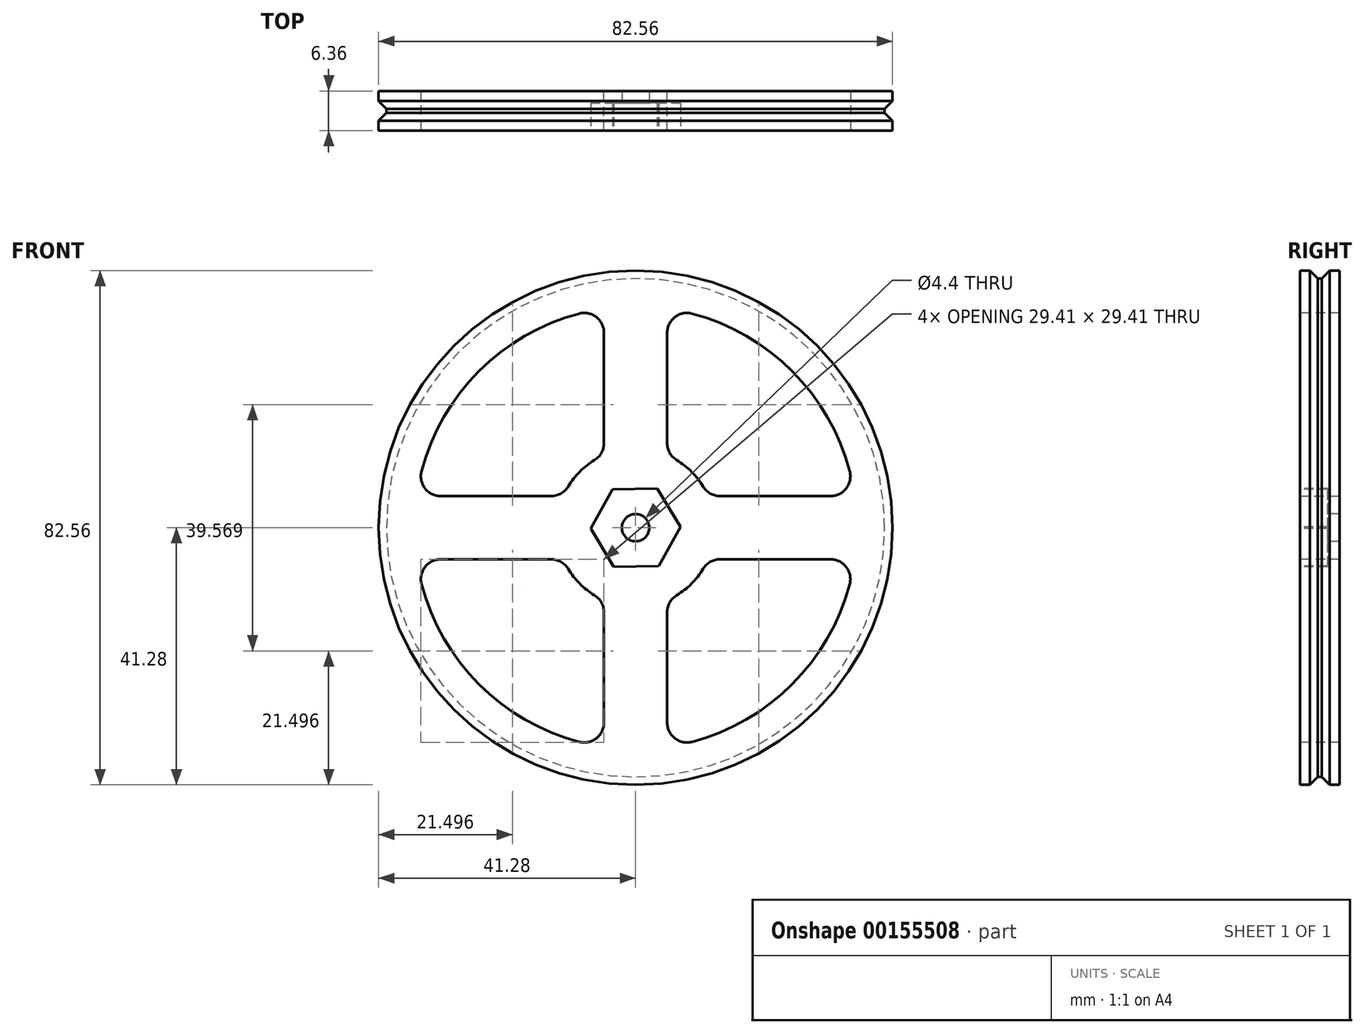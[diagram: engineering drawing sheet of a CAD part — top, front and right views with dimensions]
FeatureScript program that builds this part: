
annotation { "Feature Type Name" : "Feature", "Feature Type Description" : "" }
export const myFeature = defineFeature(function(context is Context, id is Id, definition is map)
    precondition{}
    {
        {
            var Q0;
            Q0=qCreatedBy(makeId("Front.planeOp"),FACE);
            var sketch = newSketch(context, id + "F0", { "sketchPlane" : qUnion([Q0])});
            skCircle(sketch, "E0", {"center": v(0, 0) * mm, "radius": 40 * mm});
            skCircle(sketch, "E1.0", {"center": v(0, 0) * mm, "radius": 41.28 * mm});
            skCircle(sketch, "E2.cCircle", {"center": v(0, 0) * mm, "radius": 6.35 * mm, "construction": true});
            skLineSegment(sketch, "E2.0", {"start": v(-3.67, 6.35) * mm, "end": v(3.67, 6.35) * mm});
            skLineSegment(sketch, "E2.1", {"start": v(3.67, 6.35) * mm, "end": v(7.33, 0) * mm});
            skLineSegment(sketch, "E2.2", {"start": v(7.33, 0) * mm, "end": v(3.67, -6.35) * mm});
            skLineSegment(sketch, "E2.3", {"start": v(3.67, -6.35) * mm, "end": v(-3.67, -6.35) * mm});
            skLineSegment(sketch, "E2.4", {"start": v(-3.67, -6.35) * mm, "end": v(-7.33, 0) * mm});
            skLineSegment(sketch, "E2.5", {"start": v(-7.33, 0) * mm, "end": v(-3.67, 6.35) * mm});
            skPoint(sketch, "E2.0.midPoint", {"position": v(0, 6.35) * mm});
            skSolve(sketch);
        }
        {
            var Q0;
            Q0=makeQuery(id+"F0.imprint","IMPRINT",FACE,{"disambiguationData":[TD([[makeQuery(id+"F0.imprint","IMPRINT",EDGE,{"derivedFrom":sQuery(id+"F0.wireOp",EDGE,"E0")}),1.0]])]});
            var Q1;
            Q1=makeQuery(id+"F0.imprint","IMPRINT",FACE,{"disambiguationData":[TD([[makeQuery(id+"F0.imprint","IMPRINT",EDGE,{"derivedFrom":sQuery(id+"F0.wireOp",EDGE,"E0")}),-1.0]])]});
            var Q2;
            Q2=makeQuery(id+"F0.imprint","IMPRINT",FACE,{"disambiguationData":[TD([[makeQuery(id+"F0.imprint","IMPRINT",EDGE,{"derivedFrom":sQuery(id+"F0.wireOp",EDGE,"E2.0")}),-1.0]])]});
            extrude(context, id + "F1", {"entities" : qUnion([Q0, Q1, Q2]), "endBound" : BoundingType.SYMMETRIC, "depth" : 6.35 * mm});
        }
        {
            var Q0;
            Q0=makeQuery(id+"F1.opExtrude","CAP_FACE",FACE,{"disambiguationData":[OSD([sQuery(id+"F0.wireOp",EDGE,"E1.0")])],"isStart":false});
            var sketch = newSketch(context, id + "F2", { "sketchPlane" : qUnion([Q0])});
            skCircle(sketch, "E3.cCircle", {"center": v(0, 0) * mm, "radius": 6.22 * mm, "construction": true});
            skLineSegment(sketch, "E3.0", {"start": v(3.49, 6.28) * mm, "end": v(7.18, 0.12) * mm});
            skLineSegment(sketch, "E3.1", {"start": v(7.18, 0.12) * mm, "end": v(3.7, -6.16) * mm});
            skLineSegment(sketch, "E3.2", {"start": v(3.7, -6.16) * mm, "end": v(-3.49, -6.28) * mm});
            skLineSegment(sketch, "E3.3", {"start": v(-3.49, -6.28) * mm, "end": v(-7.18, -0.12) * mm});
            skLineSegment(sketch, "E3.4", {"start": v(-7.18, -0.12) * mm, "end": v(-3.7, 6.16) * mm});
            skLineSegment(sketch, "E3.5", {"start": v(-3.7, 6.16) * mm, "end": v(3.49, 6.28) * mm});
            skPoint(sketch, "E3.0.midPoint", {"position": v(5.34, 3.2) * mm});
            skSolve(sketch);
        }
        {
            var Q0;
            Q0 = qSketchRegion(id + "F2", true);
            extrude(context, id + "F3", {"entities" : qUnion([Q0]), "operationType" : NewBodyOperationType.REMOVE, "oppositeDirection" : true, "depth" : 4.44 * mm});
        }
        {
            var Q0;
            Q0=makeQuery(id+"F1.opExtrude","CAP_FACE",FACE,{"disambiguationData":[OSD([sQuery(id+"F0.wireOp",EDGE,"E1.0"),sQuery(id+"F0.wireOp",EDGE,"E2.0"),sQuery(id+"F0.wireOp",EDGE,"E2.1"),sQuery(id+"F0.wireOp",EDGE,"E2.2"),sQuery(id+"F0.wireOp",EDGE,"E2.3"),sQuery(id+"F0.wireOp",EDGE,"E2.4"),sQuery(id+"F0.wireOp",EDGE,"E2.5")])],"isStart":false});
            var sketch = newSketch(context, id + "F4", { "sketchPlane" : qUnion([Q0])});
            skCircle(sketch, "E4", {"center": v(0, 0) * mm, "radius": 35.56 * mm});
            skCircle(sketch, "E5.0", {"center": v(0, 0) * mm, "radius": 12.7 * mm});
            skLineSegment(sketch, "E6", {"start": v(0, -12.7) * mm, "end": v(0, -35.56) * mm});
            skLineSegment(sketch, "E7.0", {"start": v(-5.08, -11.64) * mm, "end": v(-5.08, -35.2) * mm});
            skLineSegment(sketch, "E8.0", {"start": v(5.08, -11.64) * mm, "end": v(5.08, -35.2) * mm});
            skLineSegment(sketch, "E9.1.0", {"start": v(11.64, -5.08) * mm, "end": v(35.2, -5.08) * mm});
            skLineSegment(sketch, "E9.1.1", {"start": v(11.64, 5.08) * mm, "end": v(35.2, 5.08) * mm});
            skLineSegment(sketch, "E9.2.0", {"start": v(5.08, 11.64) * mm, "end": v(5.08, 35.2) * mm});
            skLineSegment(sketch, "E9.2.1", {"start": v(-5.08, 11.64) * mm, "end": v(-5.08, 35.2) * mm});
            skLineSegment(sketch, "E9.3.0", {"start": v(-11.64, 5.08) * mm, "end": v(-35.2, 5.08) * mm});
            skLineSegment(sketch, "E9.3.1", {"start": v(-11.64, -5.08) * mm, "end": v(-35.2, -5.08) * mm});
            skSolve(sketch);
        }
        {
            var Q0;
            {var subQ0=sQuery(id+"F4.wireOp",EDGE,"E7.0");Q0=makeQuery(id+"F4.imprint","IMPRINT",FACE,{"disambiguationData":[TD([[makeQuery(id+"F4.imprint","IMPRINT",EDGE,{"derivedFrom":subQ0}),-1.0]])]});}
            var Q1;
            {var subQ0=sQuery(id+"F4.wireOp",EDGE,"E9.2.1");Q1=makeQuery(id+"F4.imprint","IMPRINT",FACE,{"disambiguationData":[TD([[makeQuery(id+"F4.imprint","IMPRINT",EDGE,{"derivedFrom":subQ0}),1.0]])]});}
            var Q2;
            {var subQ0=sQuery(id+"F4.wireOp",EDGE,"E9.1.1");Q2=makeQuery(id+"F4.imprint","IMPRINT",FACE,{"disambiguationData":[TD([[makeQuery(id+"F4.imprint","IMPRINT",EDGE,{"derivedFrom":subQ0}),1.0]])]});}
            var Q3;
            {var subQ0=sQuery(id+"F4.wireOp",EDGE,"E8.0");Q3=makeQuery(id+"F4.imprint","IMPRINT",FACE,{"disambiguationData":[TD([[makeQuery(id+"F4.imprint","IMPRINT",EDGE,{"derivedFrom":subQ0}),1.0]])]});}
            extrude(context, id + "F5", {"entities" : qUnion([Q0, Q1, Q2, Q3]), "operationType" : NewBodyOperationType.REMOVE, "endBound" : BoundingType.THROUGH_ALL, "oppositeDirection" : true, "depth" : 25.4 * mm});
        }
        {
            var Q0;
            Q0=makeQuery(id+"F5.boolean.opBoolean","COPY",EDGE,{"derivedFrom":makeQuery(id+"F5.opExtrude","SWEPT_EDGE",EDGE,{"disambiguationData":[OSD([sQuery(id+"F4.wireOp",EDGE,"E4"),sQuery(id+"F4.wireOp",EDGE,"27957d35-a56d-4cfa-9457-b1a0cf56e145.3.0")])]})});
            var Q1;
            Q1=makeQuery(id+"F5.boolean.opBoolean","COPY",EDGE,{"derivedFrom":makeQuery(id+"F5.opExtrude","SWEPT_EDGE",EDGE,{"disambiguationData":[OSD([sQuery(id+"F4.wireOp",EDGE,"E4"),sQuery(id+"F4.wireOp",EDGE,"e348a229-b992-494f-8d39-545bbdace99f.0")])]})});
            var Q2;
            Q2=makeQuery(id+"F5.boolean.opBoolean","COPY",EDGE,{"derivedFrom":makeQuery(id+"F5.opExtrude","SWEPT_EDGE",EDGE,{"disambiguationData":[OSD([sQuery(id+"F4.wireOp",EDGE,"E5.0"),sQuery(id+"F4.wireOp",EDGE,"27957d35-a56d-4cfa-9457-b1a0cf56e145.1.1")])]})});
            var Q3;
            Q3=makeQuery(id+"F5.boolean.opBoolean","COPY",EDGE,{"derivedFrom":makeQuery(id+"F5.opExtrude","SWEPT_EDGE",EDGE,{"disambiguationData":[OSD([sQuery(id+"F4.wireOp",EDGE,"E5.0"),sQuery(id+"F4.wireOp",EDGE,"27957d35-a56d-4cfa-9457-b1a0cf56e145.2.0")])]})});
            var Q4;
            Q4=makeQuery(id+"F5.boolean.opBoolean","COPY",EDGE,{"derivedFrom":makeQuery(id+"F5.opExtrude","SWEPT_EDGE",EDGE,{"disambiguationData":[OSD([sQuery(id+"F4.wireOp",EDGE,"E4"),sQuery(id+"F4.wireOp",EDGE,"27957d35-a56d-4cfa-9457-b1a0cf56e145.2.1")])]})});
            var Q5;
            Q5=makeQuery(id+"F5.boolean.opBoolean","COPY",EDGE,{"derivedFrom":makeQuery(id+"F5.opExtrude","SWEPT_EDGE",EDGE,{"disambiguationData":[OSD([sQuery(id+"F4.wireOp",EDGE,"E5.0"),sQuery(id+"F4.wireOp",EDGE,"27957d35-a56d-4cfa-9457-b1a0cf56e145.2.1")])]})});
            var Q6;
            Q6=makeQuery(id+"F5.boolean.opBoolean","COPY",EDGE,{"derivedFrom":makeQuery(id+"F5.opExtrude","SWEPT_EDGE",EDGE,{"disambiguationData":[OSD([sQuery(id+"F4.wireOp",EDGE,"E4"),sQuery(id+"F4.wireOp",EDGE,"27957d35-a56d-4cfa-9457-b1a0cf56e145.2.0")])]})});
            var Q7;
            Q7=makeQuery(id+"F5.boolean.opBoolean","COPY",EDGE,{"derivedFrom":makeQuery(id+"F5.opExtrude","SWEPT_EDGE",EDGE,{"disambiguationData":[OSD([sQuery(id+"F4.wireOp",EDGE,"E4"),sQuery(id+"F4.wireOp",EDGE,"27957d35-a56d-4cfa-9457-b1a0cf56e145.1.1")])]})});
            var Q8;
            Q8=makeQuery(id+"F5.boolean.opBoolean","COPY",EDGE,{"derivedFrom":makeQuery(id+"F5.opExtrude","SWEPT_EDGE",EDGE,{"disambiguationData":[OSD([sQuery(id+"F4.wireOp",EDGE,"E4"),sQuery(id+"F4.wireOp",EDGE,"27957d35-a56d-4cfa-9457-b1a0cf56e145.1.0")])]})});
            var Q9;
            Q9=makeQuery(id+"F5.boolean.opBoolean","COPY",EDGE,{"derivedFrom":makeQuery(id+"F5.opExtrude","SWEPT_EDGE",EDGE,{"disambiguationData":[OSD([sQuery(id+"F4.wireOp",EDGE,"E5.0"),sQuery(id+"F4.wireOp",EDGE,"27957d35-a56d-4cfa-9457-b1a0cf56e145.3.1")])]})});
            var Q10;
            Q10=makeQuery(id+"F5.boolean.opBoolean","COPY",EDGE,{"derivedFrom":makeQuery(id+"F5.opExtrude","SWEPT_EDGE",EDGE,{"disambiguationData":[OSD([sQuery(id+"F4.wireOp",EDGE,"E5.0"),sQuery(id+"F4.wireOp",EDGE,"0dbcb386-fed9-4ae0-a355-918e704f70ac.0")])]})});
            var Q11;
            Q11=makeQuery(id+"F5.boolean.opBoolean","COPY",EDGE,{"derivedFrom":makeQuery(id+"F5.opExtrude","SWEPT_EDGE",EDGE,{"disambiguationData":[OSD([sQuery(id+"F4.wireOp",EDGE,"E4"),sQuery(id+"F4.wireOp",EDGE,"0dbcb386-fed9-4ae0-a355-918e704f70ac.0")])]})});
            var Q12;
            Q12=makeQuery(id+"F5.boolean.opBoolean","COPY",EDGE,{"derivedFrom":makeQuery(id+"F5.opExtrude","SWEPT_EDGE",EDGE,{"disambiguationData":[OSD([sQuery(id+"F4.wireOp",EDGE,"E4"),sQuery(id+"F4.wireOp",EDGE,"27957d35-a56d-4cfa-9457-b1a0cf56e145.3.1")])]})});
            var Q13;
            Q13=makeQuery(id+"F5.boolean.opBoolean","COPY",EDGE,{"derivedFrom":makeQuery(id+"F5.opExtrude","SWEPT_EDGE",EDGE,{"disambiguationData":[OSD([sQuery(id+"F4.wireOp",EDGE,"E5.0"),sQuery(id+"F4.wireOp",EDGE,"27957d35-a56d-4cfa-9457-b1a0cf56e145.3.0")])]})});
            var Q14;
            Q14=makeQuery(id+"F5.boolean.opBoolean","COPY",EDGE,{"derivedFrom":makeQuery(id+"F5.opExtrude","SWEPT_EDGE",EDGE,{"disambiguationData":[OSD([sQuery(id+"F4.wireOp",EDGE,"E5.0"),sQuery(id+"F4.wireOp",EDGE,"e348a229-b992-494f-8d39-545bbdace99f.0")])]})});
            var Q15;
            Q15=makeQuery(id+"F5.boolean.opBoolean","COPY",EDGE,{"derivedFrom":makeQuery(id+"F5.opExtrude","SWEPT_EDGE",EDGE,{"disambiguationData":[OSD([sQuery(id+"F4.wireOp",EDGE,"E5.0"),sQuery(id+"F4.wireOp",EDGE,"27957d35-a56d-4cfa-9457-b1a0cf56e145.1.0")])]})});
            fillet(context, id + "F6", {"entities" : qUnion([Q0, Q1, Q2, Q3, Q4, Q5, Q6, Q7, Q8, Q9, Q10, Q11, Q12, Q13, Q14, Q15]), "radius" : 3.17 * mm, "tangentPropagation" : true, "allowEdgeOverflow" : false});
        }
        {
            var Q0;
            Q0=makeQuery(id+"F3.boolean.opBoolean","COPY",FACE,{"derivedFrom":makeQuery(id+"F3.opExtrude","CAP_FACE",FACE,{"disambiguationData":[OSD([sQuery(id+"F2.wireOp",EDGE,"E3.0"),sQuery(id+"F2.wireOp",EDGE,"E3.1"),sQuery(id+"F2.wireOp",EDGE,"E3.2"),sQuery(id+"F2.wireOp",EDGE,"E3.3"),sQuery(id+"F2.wireOp",EDGE,"E3.4"),sQuery(id+"F2.wireOp",EDGE,"E3.5")])],"isStart":false})});
            var sketch = newSketch(context, id + "F7", { "sketchPlane" : qUnion([Q0])});
            skPoint(sketch, "E10", {"position": v(0, 0) * mm});
            skSolve(sketch);
        }
        {
            var Q0;
            Q0=sQuery(id+"F7.wireOp",VERTEX,"E10");
            var Q1;
            Q1=makeQuery(id+"F1.opExtrude","SWEPT_BODY",BODY,{"disambiguationData":[OSD([sQuery(id+"F0.wireOp",EDGE,"E1.0")])]});
            hole(context, id + "F8", {"style" : HoleStyle.SIMPLE, "endStyle" : HoleEndStyle.THROUGH, "standardTappedOrClearance" : lookupTablePath({ "standard" : "ISO", "fit" : "Normal", "size" : "M4", "type" : "Clearance" }), "standardBlindInLast" : lookupTablePath({ "fit" : "Standard", "standard" : "ISO", "size" : "M4", "type" : "Clearance" }), "holeDiameter" : 4.4 * mm, "locations" : qUnion([Q0]), "scope" : qUnion([Q1]), "isTappedThrough" : true});
        }
        {
            var Q0;
            Q0=qCreatedBy(makeId("Front.planeOp"),FACE);
            var sketch = newSketch(context, id + "F9", { "sketchPlane" : qUnion([Q0])});
            skCircle(sketch, "E11", {"center": v(0, 0) * mm, "radius": 40 * mm});
            skCircle(sketch, "E12.0", {"center": v(0, 0) * mm, "radius": 41.28 * mm});
            skSolve(sketch);
        }
        {
            var Q0;
            Q0 = qSketchRegion(id + "F9", true);
            extrude(context, id + "F10", {"entities" : qUnion([Q0]), "operationType" : NewBodyOperationType.REMOVE, "endBound" : BoundingType.SYMMETRIC, "oppositeDirection" : true, "depth" : 3.17 * mm});
        }
        {
            var Q0;
            Q0=makeQuery(id+"F10.boolean.opBoolean","COPY",EDGE,{"derivedFrom":makeQuery(id+"F10.opExtrude","CAP_EDGE",EDGE,{"disambiguationData":[OSD([sQuery(id+"F9.wireOp",EDGE,"E11")])],"isStart":false})});
            var Q1;
            Q1=makeQuery(id+"F10.boolean.opBoolean","COPY",EDGE,{"derivedFrom":makeQuery(id+"F10.opExtrude","CAP_EDGE",EDGE,{"disambiguationData":[OSD([sQuery(id+"F9.wireOp",EDGE,"E11")])],"isStart":true})});
            chamfer(context, id + "F11", {"entities" : qUnion([Q0, Q1]), "width" : 1.27 * mm, "tangentPropagation" : true});
        }
    });
